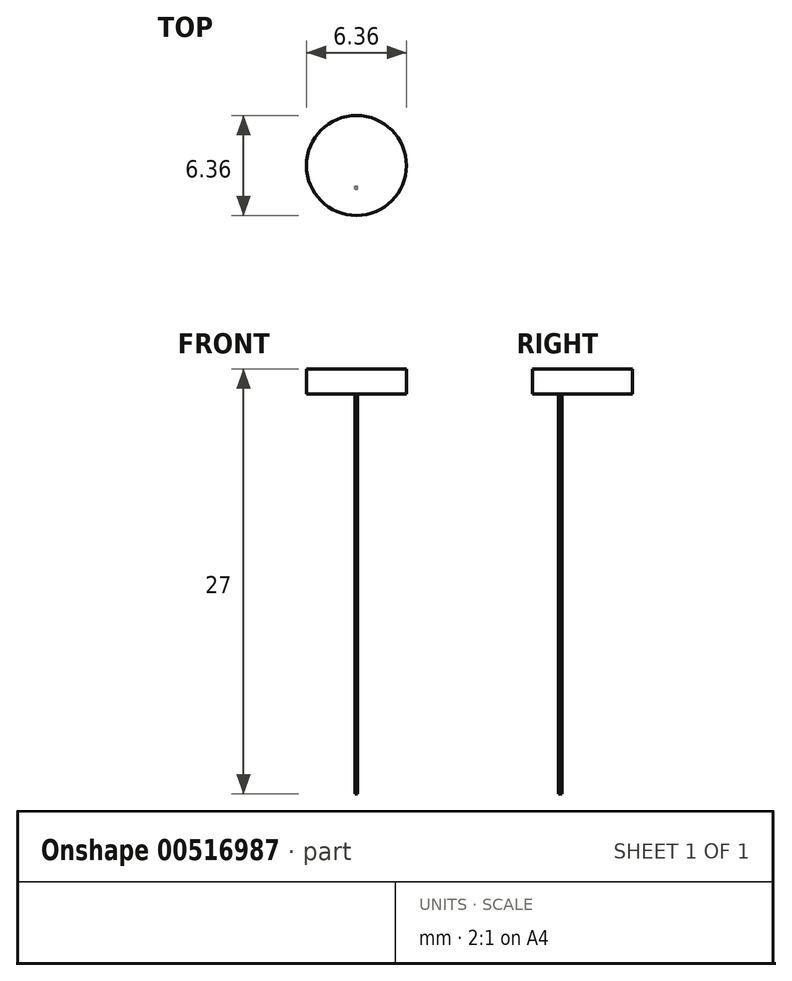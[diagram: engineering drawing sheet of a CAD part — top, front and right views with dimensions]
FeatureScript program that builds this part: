
annotation { "Feature Type Name" : "Feature", "Feature Type Description" : "" }
export const myFeature = defineFeature(function(context is Context, id is Id, definition is map)
    precondition{}
    {
        {
            var Q0;
            Q0=qCreatedBy(makeId("Top.planeOp"),FACE);
            var sketch = newSketch(context, id + "F0", { "sketchPlane" : qUnion([Q0])});
            skCircle(sketch, "E0", {"center": v(0, 0) * mm, "radius": 3.18 * mm});
            skSolve(sketch);
        }
        {
            var Q0;
            Q0 = qSketchRegion(id + "F0", true);
            extrude(context, id + "F1", {"entities" : qUnion([Q0]), "depth" : 1.6 * mm, "offsetDistance" : 25.4 * mm});
        }
        {
            var Q0;
            Q0=makeQuery(id+"F1.opExtrude","CAP_FACE",FACE,{"disambiguationData":[OSD([sQuery(id+"F0.wireOp",EDGE,"E0")])],"isStart":true});
            var sketch = newSketch(context, id + "F2", { "sketchPlane" : qUnion([Q0])});
            skLineSegment(sketch, "E1.bottom", {"start": v(-0.1, 1.51) * mm, "end": v(0.08, 1.51) * mm});
            skLineSegment(sketch, "E1.top", {"start": v(-0.1, 1.3) * mm, "end": v(0.08, 1.3) * mm});
            skLineSegment(sketch, "E1.left", {"start": v(-0.1, 1.51) * mm, "end": v(-0.1, 1.3) * mm});
            skLineSegment(sketch, "E1.right", {"start": v(0.08, 1.51) * mm, "end": v(0.08, 1.3) * mm});
            skSolve(sketch);
        }
        {
            var Q0;
            Q0 = qSketchRegion(id + "F2", true);
            extrude(context, id + "F3", {"entities" : qUnion([Q0]), "operationType" : NewBodyOperationType.ADD, "depth" : 25.4 * mm, "offsetDistance" : 25.4 * mm});
        }
    });
